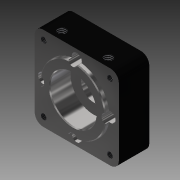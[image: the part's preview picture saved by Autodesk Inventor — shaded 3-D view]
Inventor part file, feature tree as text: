
AUTODESK INVENTOR PART (.ipt)
format: ipt  version: 2013 (Build 170138000, 138)  size: 233,984 bytes
history: native  units: in
note: dims shown in document units (in); Inventor stores cm internally (conversion verified against a paired STEP export)
features: thread x8, extrude x5, sketch x3, fillet x1, chamfer x1
ambient origin geometry x8: Origin, YZ Plane, XZ Plane, XY Plane, X Axis, Y Axis, Z Axis, Center Point
bodies: Solid1 (feature_tree)
feature tree (18):
  sketch  "Sketch1"  dims[d0=0.75in d2=2.5in]
  extrude  "Extrusion1"  Depth=2.5in
  extrude  "Extrusion2"  Depth=0.185in
  extrude  "Extrusion3"  Depth=1.0in
  fillet  "Fillet1"  Radius=1.0in
  chamfer  "Chamfer1"  Distance=1.0in
  thread  "Thread1"  [1 undecoded]
  thread  "Thread2"  [1 undecoded]
  thread  "Thread3"  [1 undecoded]
  thread  "Thread4"  [1 undecoded]
  extrude  "Extrusion4"  Depth=0.1575in
  extrude  "Extrusion5"  Depth=0.97in
  thread  "Thread5"  [1 undecoded]
  thread  "Thread6"  [1 undecoded]
  thread  "Thread7"  [1 undecoded]
  thread  "Thread8"  [1 undecoded]
  sketch  "Sketch2"  dims[d3=2.5in d4=0.185in]
  sketch  "Sketch3"  dims[d5=1.94in d6=1.0in d7=1.0in d8=1.0in d9=1.0in d10=1.375in d11=0.902in d12=0.0in d13=2.126in d14=2.126in d15=0.1575in d16=0.97in d17=0.3in d18=0.5in d19=0.0in d20=0.1181in d21=0.0in d22=0.25in d23=0.025in d24=0.125in d25=45.0deg d26=0.167in d27=1.0in d28=0.0in d29=1.0in d30=0.0in d31=1.0in d32=0.0in d33=1.0in d34=0.0in d35=1.378in d37=0.25in d38=0.652in d39=0.5in d40=0.0in d41=0.25in d43=0.652in d44=1.378in d45=0.5in d46=0.0in d47=1.0in d48=0.0in d49=1.0in d50=0.0in d51=1.0in d52=0.0in d53=1.0in d54=0.0in]
note: 8 required parameter values undecoded (feature->parameter linkage not recoverable at this tier; creation-order binding heuristic only, values carry confidence <= 0.55)
